# Revit family: Lift_Wheelchair_Ascension_Virtuoso-Portable
name_source: partatom
category: Specialty Equipment
units: mm (PartAtom-declared; Revit-internal decimal feet)

## family parameters
Always vertical = Yes
Classification Number = 23.50.05.14.17.11
Cut with Voids When Loaded = No
Enable Cutting in Views = No
Maintain Annotation Orientation = No
Part Type = Normal
Room Calculation Point = No
Round Connector Dimension = Use Diameter
Shared = No
Work Plane-Based = No

## types (1)
- as Specified
    Assembly Code = D1010310
    Available Options = as Specified
    Capacity = 1 Person Occupancy @ 750 lbs
    Clearance Depth = 0' - 0"
    Clearance Height = 0' - 0"
    Default Elevation = 0' - 0"
    Description = Ascension Portable Wheelchair Vertical Lift - Virtuoso 5460P as Specified
    Electrical_Amperage = 13 A
    Electrical_Frequency = 60 Hz
    Electrical_Phase = 1
    Electrical_Voltage = 120 V
    Expected Lifespan (Years) = 0
    Keynote = 14420
    Lift Height = 5' - 0"
    Lift Travel Speed = 7 ft/min
    Maintenance Schedule (Months) = 0
    Manufacturer = Ascension
    Manufacturer Fax = 520-881-4983
    Manufacturer Website = http://www.wheelchairlift.com
    Max Height = 0' - 0"
    Model = Virtuoso 5460P
    Platform Clear Length = 4' - 6 1/4"
    Platform Clear Width = 3' - 0"
    Product Data = http://www.arcat.com
    Revision = R1_2015-08
    Sales Information = http://www.wheelchairlift.com
    Specification = http://www.arcat.com
    Standards Conformance = ADAAG  ;  ASME 17.1 1996, A18.1  ;  ANSI 117.1
    Type Comments = Unit can collapse to fit through 36'' entrances
    URL = http://www.wheelchairlift.com
    Unit Height = 3' - 8"
    Unit Length = 5' - 4 3/4"
    Unit Weight = 1025
    Unit Width = 3' - 11 1/4"
    Warranty Duration (Years) = 0

## geometry (parser evidence)
native form markers: Sweep x7
no freeform markers — native parametric forms only
